# Revit family: DockLeveler_MDC-M-Series_BlueGiant_Edge-of-Dock
name_source: partatom
category: Generic Models
units: mm (PartAtom-declared; Revit-internal decimal feet)

## family parameters
Can host rebar = No
Classification Number = 23.50.70.14.14
Cut with Voids When Loaded = No
Host = Face
Maintain Annotation Orientation = No
Part Type = Normal
Room Calculation Point = No
Round Connector Dimension = Use Diameter
Shared = No

## types (7) — shared parameters
Assembly Code = E1030300
Construction Details = http://www.arcat.com
Deck Length = 2' - 3"
Default Elevation = 0' - 0"
Fixture Material = Metal - Blue Giant - Finish as Specified
Green Building-LEED = http://www.arcat.com
Installation-Fabrication = http://www.bluegiant.com
Keynote = 11160
Manufacturer = Blue Giant Equipment Corp.
Manufacturer Fax = 905-457-2313
Manufacturer Website = http://www.bluegiant.com
Product Data = http://www.arcat.com
Revision = R1_06_2014
Sales Information = http://www.bluegiant.com
Send Message = http://www.arcat.com
SpecWizard = http://www.arcat.com
Specification = http://www.arcat.com
URL = http://www.bluegiant.com
Unit Depth = 1' - 4"
Unit Height = 1' - 5 1/2"
zero-valued in all types: Expected Lifespan (Years), Maintenance Schedule (Months), Warranty Duration (Years)

## per-type parameters (varying)
| type | Capacity | Deck Width | Description | Unit Width |
| MDC7825M | 30000 lbs | 6' - 6" | Blue Giant MDC7825M Mechanical EOD Dock Leveler as Specified | 9' - 4" |
| MDC7230M | 30000 lbs | 6' - 0" | Blue Giant MDC7230M Mechanical EOD Dock Leveler as Specified | 8' - 10" |
| MDC7225M | 25000 lbs | 6' - 0" | Blue Giant MDC7225M Mechanical EOD Dock Leveler as Specified | 8' - 10" |
| MDC7220M | 20000 lbs | 6' - 0" | Blue Giant MDC7220M Mechanical EOD Dock Leveler as Specified | 8' - 10" |
| MDC6630M | 30000 lbs | 5' - 6" | Blue Giant MDC6630M Mechanical EOD Dock Leveler as Specified | 8' - 4" |
| MDC6625M | 25000 lbs | 5' - 6" | Blue Giant MDC6625M Mechanical EOD Dock Leveler as Specified | 8' - 4" |
| MDC6620M | 20000 lbs | 5' - 6" | Blue Giant MDC6620M Mechanical EOD Dock Leveler as Specified | 8' - 4" |

note: column(s) folded — value = type name in every type: Model

## geometry (parser evidence)
native form markers: Blend x2, Sweep x2
no freeform markers — native parametric forms only
